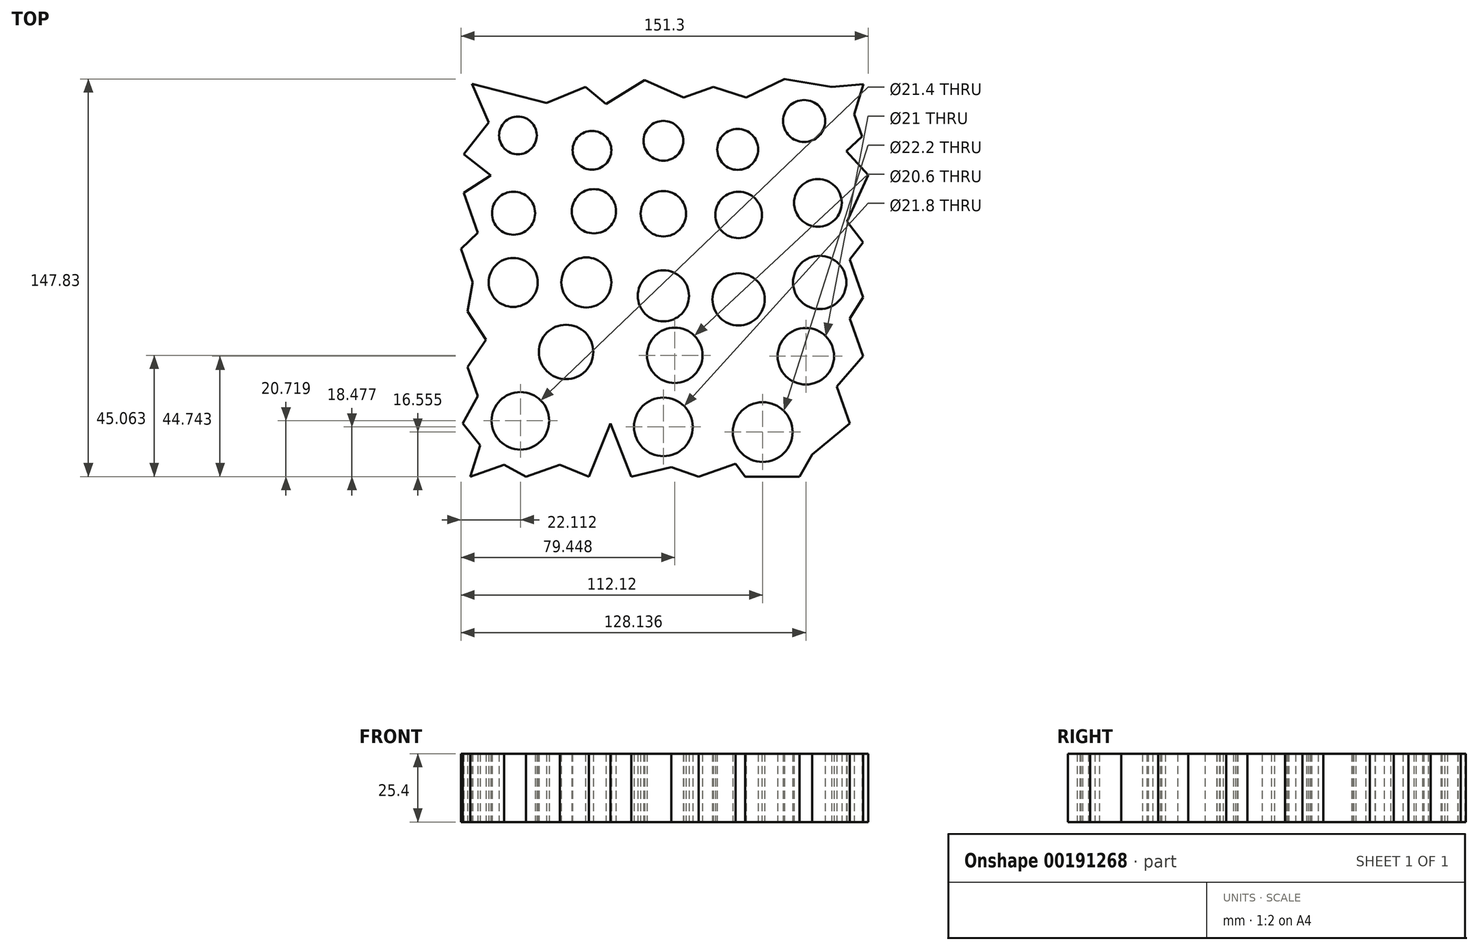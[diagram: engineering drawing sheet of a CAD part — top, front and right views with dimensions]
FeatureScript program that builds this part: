
annotation { "Feature Type Name" : "Feature", "Feature Type Description" : "" }
export const myFeature = defineFeature(function(context is Context, id is Id, definition is map)
    precondition{}
    {
        {
            var Q0;
            Q0=qCreatedBy(makeId("Top.planeOp"),FACE);
            var sketch = newSketch(context, id + "F0", { "sketchPlane" : qUnion([Q0])});
            skCircle(sketch, "E0", {"center": v(-54.03, 54.66) * mm, "radius": 7 * mm});
            skCircle(sketch, "E1", {"center": v(-26.52, 49.13) * mm, "radius": 7.2 * mm});
            skCircle(sketch, "E2", {"center": v(0, 52.65) * mm, "radius": 7.4 * mm});
            skCircle(sketch, "E3", {"center": v(27.61, 49.45) * mm, "radius": 7.6 * mm});
            skCircle(sketch, "E4", {"center": v(52.28, 60.02) * mm, "radius": 7.8 * mm});
            skCircle(sketch, "E5", {"center": v(-55.67, 25.74) * mm, "radius": 8 * mm});
            skCircle(sketch, "E6", {"center": v(-25.8, 26.46) * mm, "radius": 8.22 * mm});
            skCircle(sketch, "E7", {"center": v(0, 25.55) * mm, "radius": 8.45 * mm});
            skCircle(sketch, "E8", {"center": v(27.93, 25.1) * mm, "radius": 8.65 * mm});
            skCircle(sketch, "E9", {"center": v(57.4, 29.59) * mm, "radius": 8.85 * mm});
            skCircle(sketch, "E10", {"center": v(-55.79, 0) * mm, "radius": 9.1 * mm});
            skCircle(sketch, "E11", {"center": v(-28.63, 0) * mm, "radius": 9.3 * mm});
            skCircle(sketch, "E12", {"center": v(0, -5) * mm, "radius": 9.5 * mm});
            skCircle(sketch, "E13", {"center": v(27.93, -6.27) * mm, "radius": 9.7 * mm});
            skCircle(sketch, "E14", {"center": v(58.06, 0) * mm, "radius": 9.9 * mm});
            skCircle(sketch, "E15", {"center": v(-36.13, -25.83) * mm, "radius": 10.1 * mm});
            skCircle(sketch, "E16", {"center": v(4.23, -27.1) * mm, "radius": 10.3 * mm});
            skCircle(sketch, "E17", {"center": v(36.9, -55.61) * mm, "radius": 11.1 * mm});
            skCircle(sketch, "E18", {"center": v(52.92, -27.43) * mm, "radius": 10.5 * mm});
            skCircle(sketch, "E19", {"center": v(-53.1, -51.45) * mm, "radius": 10.7 * mm});
            skCircle(sketch, "E20", {"center": v(0, -53.7) * mm, "radius": 10.9 * mm});
            skLineSegment(sketch, "E21", {"start": v(-71.04, 73.84) * mm, "end": v(-43.37, 66.7) * mm});
            skLineSegment(sketch, "E22", {"start": v(-43.37, 66.7) * mm, "end": v(-28.99, 72.7) * mm});
            skLineSegment(sketch, "E23", {"start": v(-28.99, 72.7) * mm, "end": v(-21.35, 66.4) * mm});
            skLineSegment(sketch, "E24", {"start": v(-21.35, 66.4) * mm, "end": v(-6.9, 75.21) * mm});
            skLineSegment(sketch, "E25", {"start": v(-6.9, 75.21) * mm, "end": v(7.5, 68.78) * mm});
            skLineSegment(sketch, "E26", {"start": v(7.5, 68.78) * mm, "end": v(18.52, 72.63) * mm});
            skLineSegment(sketch, "E27", {"start": v(18.52, 72.63) * mm, "end": v(30.71, 68.78) * mm});
            skLineSegment(sketch, "E28", {"start": v(30.71, 68.78) * mm, "end": v(44.96, 75.66) * mm});
            skLineSegment(sketch, "E29", {"start": v(44.96, 75.66) * mm, "end": v(62.55, 72.63) * mm});
            skLineSegment(sketch, "E30", {"start": v(62.55, 72.63) * mm, "end": v(74.3, 73.73) * mm});
            skLineSegment(sketch, "E31", {"start": v(74.3, 73.73) * mm, "end": v(70.88, 62.53) * mm});
            skLineSegment(sketch, "E32", {"start": v(70.88, 62.53) * mm, "end": v(73.78, 54.25) * mm});
            skLineSegment(sketch, "E33", {"start": v(73.78, 54.25) * mm, "end": v(67.9, 48.84) * mm});
            skLineSegment(sketch, "E34", {"start": v(67.9, 48.84) * mm, "end": v(76.08, 39.95) * mm});
            skLineSegment(sketch, "E35", {"start": v(76.08, 39.95) * mm, "end": v(68.2, 22.66) * mm});
            skLineSegment(sketch, "E36", {"start": v(68.2, 22.66) * mm, "end": v(74.15, 14.93) * mm});
            skLineSegment(sketch, "E37", {"start": v(74.15, 14.93) * mm, "end": v(69.25, 8.5) * mm});
            skLineSegment(sketch, "E38", {"start": v(69.25, 8.5) * mm, "end": v(74.15, -5.5) * mm});
            skLineSegment(sketch, "E39", {"start": v(74.15, -5.5) * mm, "end": v(69.25, -13.43) * mm});
            skLineSegment(sketch, "E40", {"start": v(69.25, -13.43) * mm, "end": v(74.15, -27.43) * mm});
            skLineSegment(sketch, "E41", {"start": v(74.15, -27.43) * mm, "end": v(64.47, -38.7) * mm});
            skLineSegment(sketch, "E42", {"start": v(64.47, -38.7) * mm, "end": v(69.25, -52.37) * mm});
            skLineSegment(sketch, "E43", {"start": v(69.25, -52.37) * mm, "end": v(55.3, -63.96) * mm});
            skLineSegment(sketch, "E44", {"start": v(55.3, -63.96) * mm, "end": v(50.57, -72.17) * mm});
            skLineSegment(sketch, "E45", {"start": v(50.57, -72.17) * mm, "end": v(41.41, -72.17) * mm});
            skLineSegment(sketch, "E46", {"start": v(41.41, -72.17) * mm, "end": v(30.36, -72.17) * mm});
            skLineSegment(sketch, "E47", {"start": v(30.36, -72.17) * mm, "end": v(26.82, -67.36) * mm});
            skLineSegment(sketch, "E48", {"start": v(26.82, -67.36) * mm, "end": v(13.05, -72.17) * mm});
            skLineSegment(sketch, "E49", {"start": v(13.05, -72.17) * mm, "end": v(2.88, -68.7) * mm});
            skLineSegment(sketch, "E50", {"start": v(2.88, -68.7) * mm, "end": v(-11.92, -72.17) * mm});
            skLineSegment(sketch, "E51", {"start": v(-11.92, -72.17) * mm, "end": v(-19.67, -52.37) * mm});
            skLineSegment(sketch, "E52", {"start": v(-19.67, -52.37) * mm, "end": v(-27.66, -72.17) * mm});
            skLineSegment(sketch, "E53", {"start": v(-27.66, -72.17) * mm, "end": v(-38.52, -67.8) * mm});
            skLineSegment(sketch, "E54", {"start": v(-38.52, -67.8) * mm, "end": v(-51.04, -72.17) * mm});
            skLineSegment(sketch, "E55", {"start": v(-51.04, -72.17) * mm, "end": v(-59.16, -67.8) * mm});
            skLineSegment(sketch, "E56", {"start": v(-59.16, -67.8) * mm, "end": v(-71.68, -72.17) * mm});
            skLineSegment(sketch, "E57", {"start": v(-71.68, -72.17) * mm, "end": v(-68.06, -60.5) * mm});
            skLineSegment(sketch, "E58", {"start": v(-68.06, -60.5) * mm, "end": v(-74.59, -52.37) * mm});
            skLineSegment(sketch, "E59", {"start": v(-74.59, -52.37) * mm, "end": v(-68.99, -42.28) * mm});
            skLineSegment(sketch, "E60", {"start": v(-68.99, -42.28) * mm, "end": v(-72.78, -31.44) * mm});
            skLineSegment(sketch, "E61", {"start": v(-72.78, -31.44) * mm, "end": v(-65.85, -21.28) * mm});
            skLineSegment(sketch, "E62", {"start": v(-65.85, -21.28) * mm, "end": v(-72.78, -10.76) * mm});
            skLineSegment(sketch, "E63", {"start": v(-72.78, -10.76) * mm, "end": v(-70.87, 0) * mm});
            skLineSegment(sketch, "E64", {"start": v(-70.87, 0) * mm, "end": v(-75.22, 12.44) * mm});
            skLineSegment(sketch, "E65", {"start": v(-75.22, 12.44) * mm, "end": v(-68.99, 18.4) * mm});
            skLineSegment(sketch, "E66", {"start": v(-68.99, 18.4) * mm, "end": v(-74.2, 33.28) * mm});
            skLineSegment(sketch, "E67", {"start": v(-74.2, 33.28) * mm, "end": v(-64.17, 39.76) * mm});
            skLineSegment(sketch, "E68", {"start": v(-64.17, 39.76) * mm, "end": v(-74.2, 47.64) * mm});
            skLineSegment(sketch, "E69", {"start": v(-74.2, 47.64) * mm, "end": v(-64.9, 59.48) * mm});
            skLineSegment(sketch, "E70", {"start": v(-64.9, 59.48) * mm, "end": v(-71.04, 73.84) * mm});
            skSolve(sketch);
        }
        {
            var Q0;
            Q0=makeQuery(id+"F0.imprint","IMPRINT",FACE,{"disambiguationData":[TD([[makeQuery(id+"F0.imprint","IMPRINT",EDGE,{"derivedFrom":sQuery(id+"F0.wireOp",EDGE,"E0")}),-1.0]])]});
            extrude(context, id + "F1", {"entities" : qUnion([Q0]), "depth" : 25.4 * mm});
        }
    });
